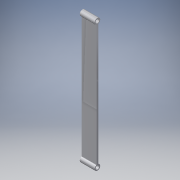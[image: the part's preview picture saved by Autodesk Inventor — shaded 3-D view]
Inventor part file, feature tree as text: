
AUTODESK INVENTOR PART (.ipt)
format: ipt  version: 2016 (Build 200138000, 138)  size: 105,984 bytes
history: native  units: in
note: dims shown in document units (in); Inventor stores cm internally (conversion verified against a paired STEP export)
features: extrude x1, sketch x1
ambient origin geometry x8: Origin, YZ Plane, XZ Plane, XY Plane, X Axis, Y Axis, Z Axis, Center Point
bodies: Solid1 (feature_tree)
feature tree (2):
  extrude  "Extrusion1"  Depth=1.0in
  sketch  "Sketch1"  dims[d0=0.125in d2=0.25in d3=0.25in d4=0.0625in d5=0.0625in d6=1.0in d7=0.0in d8=8.5in]
